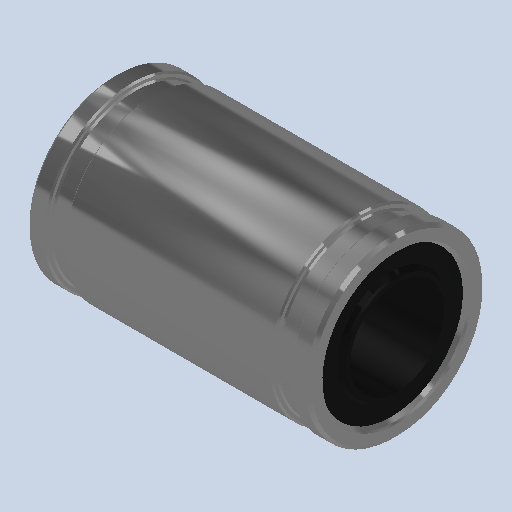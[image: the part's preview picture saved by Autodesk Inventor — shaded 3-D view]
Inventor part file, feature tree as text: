
AUTODESK INVENTOR PART (.ipt)
format: ipt  version: 2023 (Build 270158000, 158)  size: 335,360 bytes
history: native  units: in
note: dims shown in document units (in); Inventor stores cm internally (conversion verified against a paired STEP export)
features: chamfer x2, revolve x1, sketch x1
ambient origin geometry x8: Origin, YZ Plane, XZ Plane, XY Plane, X Axis, Y Axis, Z Axis, Center Point
bodies: Solid1 (feature_tree)
feature tree (4):
  revolve  "Revolution1"  [1 undecoded]
  chamfer  "Chamfer1"  Distance=0.2953in
  chamfer  "Chamfer2"  Distance=0.02in
  sketch  "Sketch1"  dims[d0=0.9252in d1=0.1575in d2=0.2953in d3=0.02in d4=0.9449in d5=0.9449in d6=0.063in d7=0.063in d8=90.0deg d9=0.01in d10=0.125in d11=45.0deg d12=0.005in d13=0.125in d14=45.0deg]
note: 1 required parameter value undecoded (feature->parameter linkage not recoverable at this tier; creation-order binding heuristic only, values carry confidence <= 0.55)
